# Revit family: Brownbuilt 406 Barge Flashing Family
name_source: partatom
category: Generic Models
revit_build: Autodesk Revit 2018 (Build: 20181011_1500(x64)
units: mm (PartAtom-declared; Revit-internal decimal feet)

## family parameters
Can host rebar = No
Cut with Voids When Loaded = No
Part Type = Normal
Room Calculation Point = No
Round Connector Dimension = Use Diameter
Shared = No

## types (1)
- Brownbuilt 406 Barge Flashing
    Brownbuilt 406 = 3.08 kg/m
    Disclaimer = Although care has been taken to ensure, to the best of our
knowledge, that all data and information contained herein
is accurate to the extent that it relates to either matters
of fact or accepted practice at the time of issue. GRS
assumes no responsibility for any errors in, or 
misinterpretation of, such data and/ or information or any
loss or damage arising from, or related to it's use.
    Girth = 550 mm
    Height = 224.53 mm
    Manufacturer = Global Roofing Solutions
    Material = ISQ 300, Galvanized Z275
    Material Thickness = 0.58 mm  [stored 0.00190289 ft]
    Model = Brownbuilt 406 Barge Flashing
    Telephone = 011 898 2900
    URL = www.globalroofs.co.za
    Width = 280 mm
    length = 1200 mm

note: [stored X ft] marks values corroborated as IEEE doubles in the binary element streams (Revit-internal decimal feet)

## geometry (parser evidence)
native form markers: Sweep x3
no freeform markers — native parametric forms only
